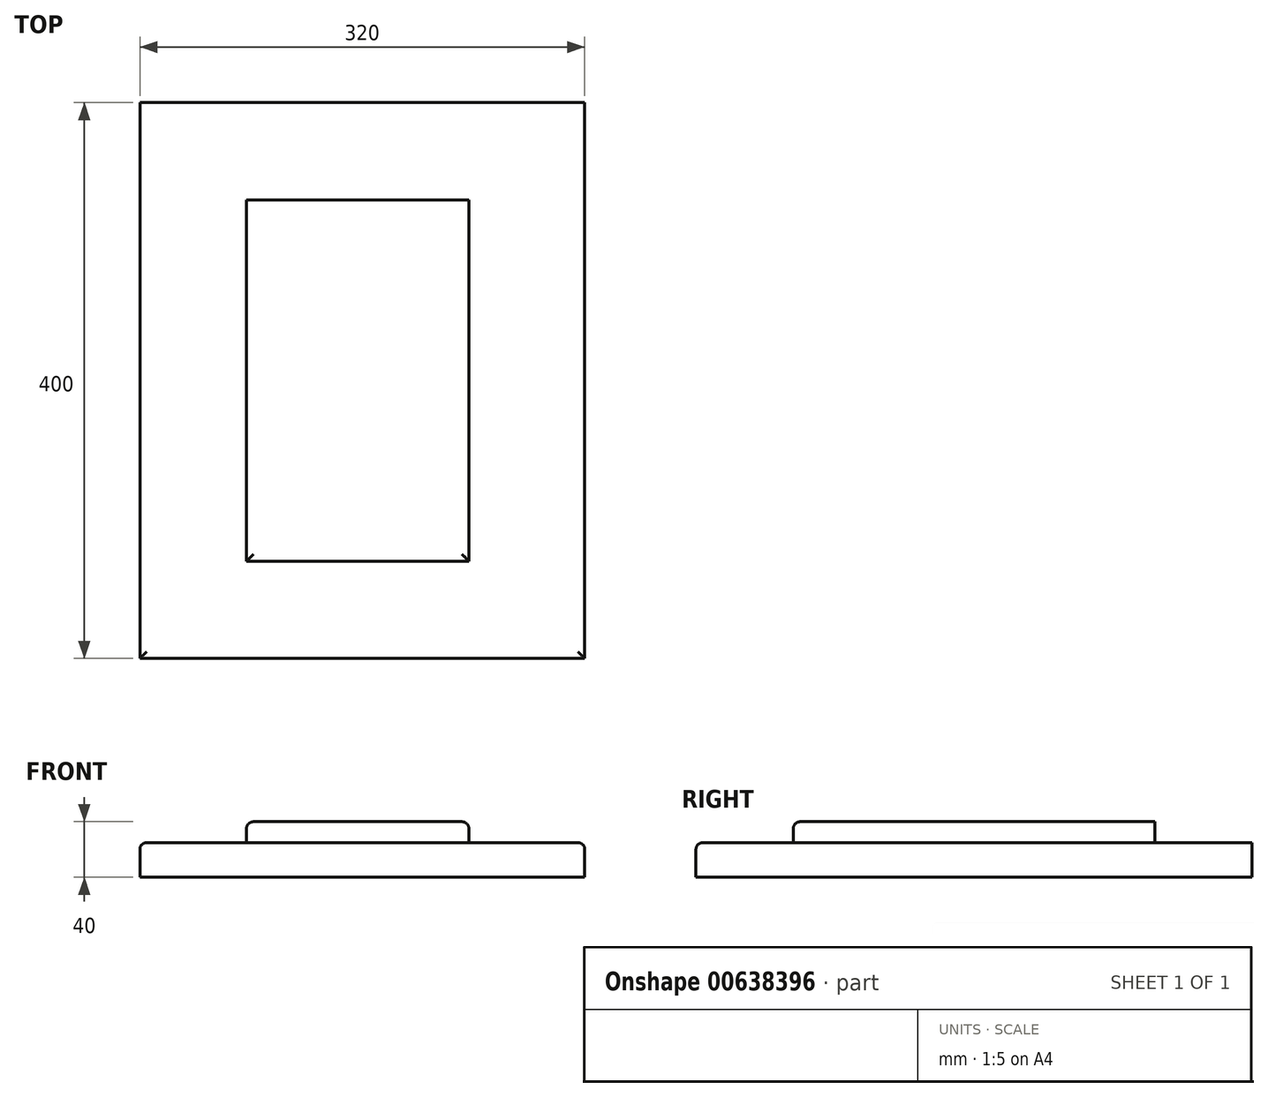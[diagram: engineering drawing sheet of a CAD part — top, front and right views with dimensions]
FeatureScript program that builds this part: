
annotation { "Feature Type Name" : "Feature", "Feature Type Description" : "" }
export const myFeature = defineFeature(function(context is Context, id is Id, definition is map)
    precondition{}
    {
        {
            var Q0;
            Q0=qCreatedBy(makeId("Top.planeOp"),FACE);
            var sketch = newSketch(context, id + "F0", { "sketchPlane" : qUnion([Q0])});
            skLineSegment(sketch, "E0.bottom", {"start": v(163.32, -200) * mm, "end": v(-156.68, -200) * mm});
            skLineSegment(sketch, "E0.top", {"start": v(163.32, 200) * mm, "end": v(-156.68, 200) * mm});
            skLineSegment(sketch, "E0.left", {"start": v(163.32, -200) * mm, "end": v(163.32, 200) * mm});
            skLineSegment(sketch, "E0.right", {"start": v(-156.68, -200) * mm, "end": v(-156.68, 200) * mm});
            skPoint(sketch, "E0.middle", {"position": v(3.32, 0) * mm});
            skSolve(sketch);
        }
        {
            var Q0;
            Q0=makeQuery(id+"F0.imprint","IMPRINT",FACE,{"disambiguationData":[TD([[makeQuery(id+"F0.imprint","IMPRINT",EDGE,{"derivedFrom":sQuery(id+"F0.wireOp",EDGE,"E0.bottom")}),-1.0]])]});
            extrude(context, id + "F1", {"entities" : qUnion([Q0]), "depth" : 25 * mm, "offsetDistance" : 25 * mm});
        }
        {
            var Q0;
            Q0=makeQuery(id+"F1.opExtrude","CAP_FACE",FACE,{"disambiguationData":[OSD([sQuery(id+"F0.wireOp",EDGE,"E0.bottom"),sQuery(id+"F0.wireOp",EDGE,"E0.top"),sQuery(id+"F0.wireOp",EDGE,"E0.left"),sQuery(id+"F0.wireOp",EDGE,"E0.right")])],"isStart":false});
            var sketch = newSketch(context, id + "F2", { "sketchPlane" : qUnion([Q0])});
            skSolve(sketch);
        }
        {
            var Q0;
            Q0=makeQuery(id+"F1.opExtrude","CAP_EDGE",EDGE,{"disambiguationData":[OSD([sQuery(id+"F0.wireOp",EDGE,"E0.right")])],"isStart":false});
            var Q1;
            Q1=makeQuery(id+"F1.opExtrude","CAP_EDGE",EDGE,{"disambiguationData":[OSD([sQuery(id+"F0.wireOp",EDGE,"E0.left")])],"isStart":false});
            var Q2;
            Q2=makeQuery(id+"F1.opExtrude","CAP_EDGE",EDGE,{"disambiguationData":[OSD([sQuery(id+"F0.wireOp",EDGE,"E0.bottom")])],"isStart":false});
            fillet(context, id + "F3", {"entities" : qUnion([Q0, Q1, Q2]), "radius" : 5 * mm, "tangentPropagation" : true, "allowEdgeOverflow" : false});
        }
        {
            var Q0;
            Q0=makeQuery(id+"F2.imprint","IMPRINT",FACE,{"disambiguationData":[TD([[makeQuery(id+"F2.imprint","IMPRINT",EDGE,{"derivedFrom":makeQuery(id+"F1.opExtrude","CAP_EDGE",EDGE,{"disambiguationData":[OSD([sQuery(id+"F0.wireOp",EDGE,"E0.bottom")])],"isStart":false})}),-1.0]])]});
            var sketch = newSketch(context, id + "F4", { "sketchPlane" : qUnion([Q0])});
            skLineSegment(sketch, "E1.bottom", {"start": v(80, -130) * mm, "end": v(-80, -130) * mm});
            skLineSegment(sketch, "E1.top", {"start": v(80, 130) * mm, "end": v(-80, 130) * mm});
            skLineSegment(sketch, "E1.left", {"start": v(80, -130) * mm, "end": v(80, 130) * mm});
            skLineSegment(sketch, "E1.right", {"start": v(-80, -130) * mm, "end": v(-80, 130) * mm});
            skPoint(sketch, "E1.middle", {"position": v(0, 0) * mm});
            skSolve(sketch);
        }
        {
            var Q0;
            Q0 = qSketchRegion(id + "F4", true);
            extrude(context, id + "F5", {"entities" : qUnion([Q0]), "operationType" : NewBodyOperationType.ADD, "depth" : 15 * mm, "offsetDistance" : 25 * mm});
        }
        {
            var Q0;
            Q0=makeQuery(id+"F5.opExtrude","CAP_EDGE",EDGE,{"disambiguationData":[OSD([sQuery(id+"F4.wireOp",EDGE,"E1.right")])],"isStart":false});
            var Q1;
            Q1=makeQuery(id+"F5.opExtrude","CAP_EDGE",EDGE,{"disambiguationData":[OSD([sQuery(id+"F4.wireOp",EDGE,"E1.bottom")])],"isStart":false});
            var Q2;
            Q2=makeQuery(id+"F5.opExtrude","CAP_EDGE",EDGE,{"disambiguationData":[OSD([sQuery(id+"F4.wireOp",EDGE,"E1.left")])],"isStart":false});
            fillet(context, id + "F6", {"entities" : qUnion([Q0, Q1, Q2]), "radius" : 5 * mm, "tangentPropagation" : true, "allowEdgeOverflow" : false});
        }
    });
